FCSTD DOCUMENT  (FreeCAD 1.2R20260429 (Git shallow))
Label: gripper-assembly
License: All rights reserved
LicenseURL: https://en.wikipedia.org/wiki/All_rights_reserved
objects: App::FeaturePython×20, App::Link×15, App::Point×1, Assembly::JointGroup×1, App::DocumentObjectGroup×1, Assembly::AssemblyObject×1
EXTERNAL_REF file=gripper-parts.FCStd obj=Body077
EXTERNAL_REF file=gripper-parts.FCStd obj=Body076
EXTERNAL_REF file=gripper-parts.FCStd obj=Part__Mirroring004
EXTERNAL_REF file=gripper-parts.FCStd obj=Body059
EXTERNAL_REF file=gripper-parts.FCStd obj=Body058
EXTERNAL_REF file=gripper-parts.FCStd obj=Body057
EXTERNAL_REF file=gripper-parts.FCStd obj=Body056
EXTERNAL_REF file=gripper-parts.FCStd obj=Body055
EXTERNAL_REF file=gripper-parts.FCStd obj=Body054
EXTERNAL_REF file=gripper-parts.FCStd obj=Part015
EXTERNAL_REF file=gripper-parts.FCStd obj=Part__Mirroring005
EXTERNAL_REF file=gripper-parts.FCStd obj=Part__Mirroring006
EXTERNAL_REF file=gripper-parts.FCStd obj=Body081
EXTERNAL_REF file=gripper-parts.FCStd obj=Body082
EXTERNAL_REF file=gripper-parts.FCStd obj=Body083

FEATURE [App::Link] Corps008
  LinkPlacement = pos=(-10,-131.392,102.994) rot=(0,0.131358,0.991335;3.14159rad)
  LinkedObject = -> <external gripper-parts.FCStd>#Body077
  Placement = pos=(-10,-131.392,102.994) rot=(0,0.131358,0.991335;3.14159rad)
FEATURE [App::Link] Corps007
  LinkPlacement = pos=(-10,-131.392,102.994) rot=(0,0.131358,0.991335;3.14159rad)
  LinkedObject = -> <external gripper-parts.FCStd>#Body076
  Placement = pos=(-10,-131.392,102.994) rot=(0,0.131358,0.991335;3.14159rad)
FEATURE [App::Link] Clone004__Mirror__5_  label="Clone004 (Mirror #5)"
  LinkPlacement = pos=(10,-190.423,103.07) rot=(0,0.03739,0.999301;3.14159rad)
  LinkedObject = -> <external gripper-parts.FCStd>#Part__Mirroring004
  Placement = pos=(10,-190.423,103.07) rot=(0,0.03739,0.999301;3.14159rad)
FEATURE [App::Link] SupportServoPivot
  LinkPlacement = pos=(-7.5,-131.392,102.994) rot=(0,0.131358,0.991335;3.14159rad)
  LinkedObject = -> <external gripper-parts.FCStd>#Body059
  Placement = pos=(-7.5,-131.392,102.994) rot=(0,0.131358,0.991335;3.14159rad)
FEATURE [App::Link] Corps005
  LinkPlacement = pos=(-26,-178.866,80.5912) rot=(0,-0.307811,0.951448;3.14159rad)
  LinkedObject = -> <external gripper-parts.FCStd>#Body058
  Placement = pos=(-26,-178.866,80.5912) rot=(0,-0.307811,0.951448;3.14159rad)
FEATURE [App::Link] Palonnier
  LinkPlacement = pos=(-26,-168.077,71.1456) rot=(0,-0.230988,0.972957;3.14159rad)
  LinkedObject = -> <external gripper-parts.FCStd>#Body057
  Placement = pos=(-26,-168.077,71.1456) rot=(0,-0.230988,0.972957;3.14159rad)
FEATURE [App::Link] Corps003
  LinkPlacement = pos=(-30,-166.397,111.227) rot=(0,0.09149,0.995806;3.14159rad)
  LinkedObject = -> <external gripper-parts.FCStd>#Body056
  Placement = pos=(-30,-166.397,111.227) rot=(0,0.09149,0.995806;3.14159rad)
FEATURE [App::Link] Corps002
  LinkPlacement = pos=(-30,-190.423,103.07) rot=(0,0.03739,0.999301;3.14159rad)
  LinkedObject = -> <external gripper-parts.FCStd>#Body055
  Placement = pos=(-30,-190.423,103.07) rot=(0,0.03739,0.999301;3.14159rad)
FEATURE [App::Link] SupportServoGripper
  LinkPlacement = pos=(-10,-201.703,81.4943) rot=(0,-0.412163,0.91111;3.14159rad)
  LinkedObject = -> <external gripper-parts.FCStd>#Body054
  Placement = pos=(-10,-201.703,81.4943) rot=(0,-0.412163,0.91111;3.14159rad)
FEATURE [App::Link] MG996
  LinkPlacement = pos=(-24.5,-108.04,39.0451) rot=(-0.577673,-0.576704,0.577673;2.09536rad)
  LinkedObject = -> <external gripper-parts.FCStd>#Part015
  Placement = pos=(-24.5,-108.04,39.0451) rot=(-0.577673,-0.576704,0.577673;2.09536rad)
FEATURE [App::Link] Body079__Mirror__6_  label="Body079 (Mirror #6)"
  LinkPlacement = pos=(10,-166.397,111.227) rot=(0,0.09149,0.995806;3.14159rad)
  LinkedObject = -> <external gripper-parts.FCStd>#Part__Mirroring005
  Placement = pos=(10,-166.397,111.227) rot=(0,0.09149,0.995806;3.14159rad)
FEATURE [App::Link] Body080__Mirror__7_  label="Body080 (Mirror #7)"
  LinkPlacement = pos=(10,-168.077,71.1456) rot=(0,-0.230988,0.972957;3.14159rad)
  LinkedObject = -> <external gripper-parts.FCStd>#Part__Mirroring006
  Placement = pos=(10,-168.077,71.1456) rot=(0,-0.230988,0.972957;3.14159rad)
FEATURE [App::Link] Corps010
  LinkPlacement = pos=(-10,-168.077,71.1456) rot=(0,-0.230988,0.972957;3.14159rad)
  LinkedObject = -> <external gripper-parts.FCStd>#Body081
  Placement = pos=(-10,-168.077,71.1456) rot=(0,-0.230988,0.972957;3.14159rad)
FEATURE [App::Link] Corps011
  LinkPlacement = pos=(0,0,0) rot=(-1,0,0;0.001678rad)
  LinkedObject = -> <external gripper-parts.FCStd>#Body082
  Placement = pos=(0,0,0) rot=(-1,0,0;0.001678rad)
FEATURE [App::Point] Origin001  label="Origine"
  Role = Origin
FEATURE [App::FeaturePython] Joint  label="Fixed032"  # Assembly joint (typed FeaturePython)
  Angle = 0
  AngleMax = 0
  AngleMin = 0
  Detach1 = false
  Detach2 = false
  Distance = 0
  Distance2 = 0
  EnableAngleMax = false
  EnableAngleMin = false
  EnableLengthMax = false
  EnableLengthMin = false
  JointType = 0 (Fixed)
  LengthMax = 0
  LengthMin = 0
  Offset2 = pos=(0,0,0) rot=(0,0,1;3.14159rad)
  Placement1 = pos=(-29.5,-18.5054,-98.3345) rot=(1,0,0;2.87979rad)
  Placement2 = pos=(19.5,-139.141,3) rot=(0,-1,0;3.14159rad)
  Reference1 = -> Corps007 [?Edge127,?Edge127]
  Reference2 = -> Corps011 [?Edge78,?Edge78]
  Suppressed = false
FEATURE [App::FeaturePython] Joint001  label="Fixed033"  # Assembly joint (typed FeaturePython)
  Angle = 0
  AngleMax = 0
  AngleMin = 0
  Detach1 = false
  Detach2 = false
  Distance = 0
  Distance2 = 0
  EnableAngleMax = false
  EnableAngleMin = false
  EnableLengthMax = false
  EnableLengthMin = false
  JointType = 0 (Fixed)
  LengthMax = 0
  LengthMin = 0
  Placement1 = pos=(-9e-16,-50.1695,-70.4616) rot=(0.57735,-0.57735,-0.57735;2.0944rad)
  Placement2 = pos=(-2.5,-50.1695,-70.4616) rot=(0.57735,-0.57735,-0.57735;2.0944rad)
  Reference1 = -> SupportServoPivot [?Edge58,?Edge58]
  Reference2 = -> Corps007 [?Edge94,?Edge94]
  Suppressed = false
FEATURE [App::FeaturePython] Joint002  label="Fixed034"  # Assembly joint (typed FeaturePython)
  Angle = 0
  AngleMax = 0
  AngleMin = 0
  Detach1 = false
  Detach2 = false
  Distance = 0
  Distance2 = 0
  EnableAngleMax = false
  EnableAngleMin = false
  EnableLengthMax = false
  EnableLengthMin = false
  JointType = 0 (Fixed)
  LengthMax = 0
  LengthMin = 0
  Placement1 = pos=(-33.5,-20.5388,-75.1547) rot=(0.57735,-0.57735,-0.57735;2.0944rad)
  Placement2 = pos=(-33.5,-20.5388,-75.1547) rot=(0.57735,-0.57735,-0.57735;2.0944rad)
  Reference1 = -> Corps008 [Edge21,Edge21]
  Reference2 = -> Corps007 [?Edge85,?Edge85]
  Suppressed = false
FEATURE [App::FeaturePython] Joint003  label="Revolute035"  # Assembly joint (typed FeaturePython)
  Angle = 0
  AngleMax = 0
  AngleMin = 0
  Detach1 = false
  Detach2 = false
  Distance = 0
  Distance2 = 0
  EnableAngleMax = false
  EnableAngleMin = false
  EnableLengthMax = false
  EnableLengthMin = false
  JointType = 1 (Revolute)
  LengthMax = 0
  LengthMin = 0
  Placement1 = pos=(-52,-15.6736,-58.9752) rot=(-0.57735,-0.57735,-0.57735;4.18879rad)
  Placement2 = pos=(-36,-15.6736,-58.9752) rot=(0.57735,-0.57735,-0.57735;2.0944rad)
  Reference1 = -> Corps005 [Edge85,Edge85]
  Reference2 = -> Corps008 [Edge93,Edge93]
  Suppressed = false
FEATURE [App::FeaturePython] GroundedJoint  # Assembly grounded joint (typed FeaturePython)
  ObjectToGround = -> Corps011
FEATURE [App::FeaturePython] Joint004  label="Revolute036"  # Assembly joint (typed FeaturePython)
  Angle = 0
  AngleMax = 0
  AngleMin = 0
  Detach1 = false
  Detach2 = false
  Distance = 0
  Distance2 = 0
  EnableAngleMax = false
  EnableAngleMin = false
  EnableLengthMax = false
  EnableLengthMin = false
  JointType = 1 (Revolute)
  LengthMax = 0
  LengthMin = 0
  Placement1 = pos=(-16,-39.201,-55.6603) rot=(-0.57735,-0.57735,-0.57735;4.18879rad)
  Placement2 = pos=(-36,-39.201,-55.6603) rot=(0.57735,-0.57735,-0.57735;2.0944rad)
  Reference1 = -> Body080__Mirror__7_ [Edge49,Edge49]
  Reference2 = -> Corps008 [Edge77,Edge77]
  Suppressed = false
FEATURE [App::FeaturePython] Joint005  label="Fixed036"  # Assembly joint (typed FeaturePython)
  Angle = 0
  AngleMax = 0
  AngleMin = 0
  Detach1 = false
  Detach2 = false
  Distance = 0
  Distance2 = 0
  EnableAngleMax = false
  EnableAngleMin = false
  EnableLengthMax = false
  EnableLengthMin = false
  JointType = 0 (Fixed)
  LengthMax = 0
  LengthMin = 0
  Offset2 = pos=(0,0,0) rot=(0,0,1;3.14159rad)
  Placement1 = pos=(-36,-56.5391,-24.1105) rot=(0.57735,-0.57735,-0.57735;2.0944rad)
  Placement2 = pos=(-16,-56.5391,-24.1105) rot=(-0.57735,0.57735,-0.57735;2.0944rad)
  Reference1 = -> Corps010 [Edge50,Edge50]
  Reference2 = -> Body080__Mirror__7_ [Edge40,Edge40]
  Suppressed = false
FEATURE [App::FeaturePython] Joint006  label="Revolute037"  # Assembly joint (typed FeaturePython)
  Angle = 0
  AngleMax = 0
  AngleMin = 0
  Detach1 = false
  Detach2 = false
  Distance = 0
  Distance2 = 0
  EnableAngleMax = false
  EnableAngleMin = false
  EnableLengthMax = false
  EnableLengthMin = false
  JointType = 1 (Revolute)
  LengthMax = 0
  LengthMin = 0
  Placement1 = pos=(-40,-36.0964,7.29411) rot=(-0.57735,-0.57735,-0.57735;4.18879rad)
  Placement2 = pos=(-56,-36.0964,7.29411) rot=(-0.57735,-0.57735,-0.57735;4.18879rad)
  Reference1 = -> Clone004__Mirror__5_ [Edge72,Edge72]
  Reference2 = -> Corps005 [Edge193,Edge193]
  Suppressed = false
FEATURE [App::FeaturePython] Joint007  label="Revolute038"  # Assembly joint (typed FeaturePython)
  Angle = 0
  AngleMax = 0
  AngleMin = 0
  Detach1 = false
  Detach2 = false
  Distance = 0
  Distance2 = 0
  EnableAngleMax = false
  EnableAngleMin = false
  EnableLengthMax = false
  EnableLengthMin = false
  JointType = 1 (Revolute)
  LengthMax = 0
  LengthMin = 0
  Placement1 = pos=(0,-36.0964,7.29411) rot=(-0.57735,-0.57735,-0.57735;4.18879rad)
  Placement2 = pos=(4,-36.0964,7.29411) rot=(-0.57735,-0.57735,-0.57735;4.18879rad)
  Reference1 = -> Corps002 [Edge72,Edge72]
  Reference2 = -> Corps005 [Edge191,Edge191]
  Suppressed = false
FEATURE [App::FeaturePython] Joint008  label="Revolute039"  # Assembly joint (typed FeaturePython)
  Angle = 0
  AngleMax = 0
  AngleMin = 0
  Detach1 = false
  Detach2 = false
  Distance = 0
  Distance2 = 0
  EnableAngleMax = false
  EnableAngleMin = false
  EnableLengthMax = false
  EnableLengthMin = false
  JointType = 1 (Revolute)
  LengthMax = 0
  LengthMin = 0
  Placement1 = pos=(-20,-34.4956,-23.997) rot=(-0.57735,-0.57735,-0.57735;4.18879rad)
  Placement2 = pos=(-56,-34.4956,-23.997) rot=(-0.57735,-0.57735,-0.57735;4.18879rad)
  Reference1 = -> Body079__Mirror__6_ [Edge87,Edge87]
  Reference2 = -> Corps005 [Edge187,Edge187]
  Suppressed = false
FEATURE [App::FeaturePython] Joint009  label="Revolute040"  # Assembly joint (typed FeaturePython)
  Angle = 0
  AngleMax = 0
  AngleMin = 0
  Detach1 = false
  Detach2 = false
  Distance = 0
  Distance2 = 0
  EnableAngleMax = false
  EnableAngleMin = false
  EnableLengthMax = false
  EnableLengthMin = false
  JointType = 1 (Revolute)
  LengthMax = 0
  LengthMin = 0
  Placement1 = pos=(-20,-61.8186,-11.463) rot=(-0.57735,-0.57735,-0.57735;4.18879rad)
  Placement2 = pos=(-20,-61.8186,-11.463) rot=(-0.57735,-0.57735,-0.57735;4.18879rad)
  Reference1 = -> Body079__Mirror__6_ [Edge86,Edge86]
  Reference2 = -> Body080__Mirror__7_ [Edge57,Edge57]
  Suppressed = false
FEATURE [App::FeaturePython] Joint010  label="Revolute041"  # Assembly joint (typed FeaturePython)
  Angle = 0
  AngleMax = 0
  AngleMin = 0
  Detach1 = false
  Detach2 = false
  Distance = 0
  Distance2 = 0
  EnableAngleMax = false
  EnableAngleMin = false
  EnableLengthMax = false
  EnableLengthMin = false
  JointType = 1 (Revolute)
  LengthMax = 0
  LengthMin = 0
  Placement1 = pos=(0,-34.4956,-23.997) rot=(-0.57735,-0.57735,-0.57735;4.18879rad)
  Placement2 = pos=(4,-34.4956,-23.997) rot=(-0.57735,-0.57735,-0.57735;4.18879rad)
  Reference1 = -> Corps003 [Edge87,Edge87]
  Reference2 = -> Corps005 [Edge185,Edge185]
  Suppressed = false
FEATURE [App::FeaturePython] Joint011  label="Revolute042"  # Assembly joint (typed FeaturePython)
  Angle = 0
  AngleMax = 0
  AngleMin = 0
  Detach1 = false
  Detach2 = false
  Distance = 0
  Distance2 = 0
  EnableAngleMax = false
  EnableAngleMin = false
  EnableLengthMax = false
  EnableLengthMin = false
  JointType = 1 (Revolute)
  LengthMax = 0
  LengthMin = 0
  Placement1 = pos=(-40,-10.5946,-17.3494) rot=(-0.57735,-0.57735,-0.57735;4.18879rad)
  Placement2 = pos=(-20,-10.5946,-24.3494) rot=(-0.57735,-0.57735,-0.57735;4.18879rad)
  Reference1 = -> SupportServoGripper [?Edge250,?Edge250]
  Reference2 = -> Clone004__Mirror__5_ [Edge71,Edge71]
  Suppressed = false
FEATURE [App::FeaturePython] Joint012  label="Revolute043"  # Assembly joint (typed FeaturePython)
  Angle = 0
  AngleMax = 0
  AngleMin = 0
  Detach1 = false
  Detach2 = false
  Distance = 0
  Distance2 = 0
  EnableAngleMax = false
  EnableAngleMin = false
  EnableLengthMax = false
  EnableLengthMin = false
  JointType = 1 (Revolute)
  LengthMax = 0
  LengthMin = 0
  Placement1 = pos=(-20,-10.5946,-47.1305) rot=(-0.57735,-0.57735,-0.57735;4.18879rad)
  Placement2 = pos=(-40,-10.5946,-40.1305) rot=(-0.57735,-0.57735,-0.57735;4.18879rad)
  Reference1 = -> Body079__Mirror__6_ [Edge88,Edge88]
  Reference2 = -> SupportServoGripper [?Edge248,?Edge248]
  Suppressed = false
FEATURE [App::FeaturePython] Joint013  label="Revolute044"  # Assembly joint (typed FeaturePython)
  Angle = 0
  AngleMax = 0
  AngleMin = 0
  Detach1 = false
  Detach2 = false
  Distance = 0
  Distance2 = 0
  EnableAngleMax = false
  EnableAngleMin = false
  EnableLengthMax = false
  EnableLengthMin = false
  JointType = 1 (Revolute)
  LengthMax = 0
  LengthMin = 0
  Placement1 = pos=(0,-10.5946,-24.3494) rot=(-0.57735,-0.57735,-0.57735;4.18879rad)
  Placement2 = pos=(20,-10.5946,-17.3494) rot=(-0.57735,-0.57735,-0.57735;4.18879rad)
  Reference1 = -> Corps002 [Edge71,Edge71]
  Reference2 = -> SupportServoGripper [Edge232,Edge232]
  Suppressed = false
FEATURE [App::FeaturePython] Joint014  label="Revolute046"  # Assembly joint (typed FeaturePython)
  Angle = 0
  AngleMax = 0
  AngleMin = 0
  Detach1 = false
  Detach2 = false
  Distance = 0
  Distance2 = 0
  EnableAngleMax = false
  EnableAngleMin = false
  EnableLengthMax = false
  EnableLengthMin = false
  JointType = 1 (Revolute)
  LengthMax = 0
  LengthMin = 0
  Placement1 = pos=(20,-10.5946,-40.1305) rot=(-0.57735,-0.57735,-0.57735;4.18879rad)
  Placement2 = pos=(0,-10.5946,-47.1305) rot=(-0.57735,-0.57735,-0.57735;4.18879rad)
  Reference1 = -> SupportServoGripper [Edge229,Edge229]
  Reference2 = -> Corps003 [Edge88,Edge88]
  Suppressed = false
FEATURE [App::FeaturePython] Joint015  label="Fixed037"  # Assembly joint (typed FeaturePython)
  Angle = 0
  AngleMax = 0
  AngleMin = 0
  Detach1 = false
  Detach2 = false
  Distance = 0
  Distance2 = 0
  EnableAngleMax = false
  EnableAngleMin = false
  EnableLengthMax = false
  EnableLengthMin = false
  JointType = 0 (Fixed)
  LengthMax = 0
  LengthMin = 0
  Offset2 = pos=(0,0,0) rot=(0,0,1;3.14159rad)
  Placement1 = pos=(3.6e-15,-56.5391,-24.1105) rot=(-0.57735,-0.57735,-0.57735;4.18879rad)
  Placement2 = pos=(16,-56.5391,-24.1105) rot=(-0.57735,-0.57735,0.57735;2.0944rad)
  Reference1 = -> Palonnier [Edge37,Edge37]
  Reference2 = -> Corps010 [Edge22,Edge22]
  Suppressed = false
FEATURE [App::FeaturePython] Joint016  label="Revolute047"  # Assembly joint (typed FeaturePython)
  Angle = 0
  AngleMax = 0
  AngleMin = 0
  Detach1 = false
  Detach2 = false
  Distance = 0
  Distance2 = 0
  EnableAngleMax = false
  EnableAngleMin = false
  EnableLengthMax = false
  EnableLengthMin = false
  JointType = 1 (Revolute)
  LengthMax = 0
  LengthMin = 0
  Placement1 = pos=(4,-61.8186,-11.463) rot=(-0.57735,-0.57735,-0.57735;4.18879rad)
  Placement2 = pos=(0,-61.8186,-11.463) rot=(-0.57735,-0.57735,-0.57735;4.18879rad)
  Reference1 = -> Palonnier [Edge50,Edge50]
  Reference2 = -> Corps003 [Edge86,Edge86]
  Suppressed = false
FEATURE [App::FeaturePython] Joint017  label="Revolute048"  # Assembly joint (typed FeaturePython)
  Angle = 0
  AngleMax = 0
  AngleMin = 0
  Detach1 = false
  Detach2 = false
  Distance = 0
  Distance2 = 0
  EnableAngleMax = false
  EnableAngleMin = false
  EnableLengthMax = false
  EnableLengthMin = false
  JointType = 1 (Revolute)
  LengthMax = 0
  LengthMin = 0
  Placement1 = pos=(14.5,-5,-16) rot=(0,0,1;0rad)
  Placement2 = pos=(-9e-16,-51.9128,-47.0778) rot=(0.57735,-0.57735,-0.57735;2.0944rad)
  Reference1 = -> MG996 [Body041.Edge51,Body041.Edge51]
  Reference2 = -> SupportServoPivot [?Edge61,?Edge61]
  Suppressed = false
FEATURE [App::FeaturePython] Joint018  label="Revolute049"  # Assembly joint (typed FeaturePython)
  Angle = 0
  AngleMax = 0
  AngleMin = 0
  Detach1 = false
  Detach2 = false
  Distance = 0
  Distance2 = 0
  EnableAngleMax = false
  EnableAngleMin = false
  EnableLengthMax = false
  EnableLengthMin = false
  JointType = 1 (Revolute)
  LengthMax = 0
  LengthMin = 0
  Placement1 = pos=(-34.5,5,-16) rot=(0,0,1;0rad)
  Placement2 = pos=(-9e-16,-7.17065,-69.4192) rot=(0.57735,-0.57735,-0.57735;2.0944rad)
  Reference1 = -> MG996 [Body041.Edge38,Body041.Edge38]
  Reference2 = -> SupportServoPivot [?Edge70,?Edge70]
  Suppressed = false
FEATURE [Assembly::JointGroup] Joints
  Group = -> [Joint,Joint001,Joint002,Joint003,GroundedJoint,Joint004,Joint005,Joint006,Joint007,Joint008,Joint009,Joint010,Joint011,Joint012,Joint013,Joint014,Joint015,Joint016,Joint017,Joint018]
FEATURE [App::Link] Corps
  LinkPlacement = pos=(-10,-131.392,102.994) rot=(0,0.131358,0.991335;3.14159rad)
  LinkedObject = -> <external gripper-parts.FCStd>#Body083
  Placement = pos=(-10,-131.392,102.994) rot=(0,0.131358,0.991335;3.14159rad)
FEATURE [App::DocumentObjectGroup] Group  label="PivotPrincipal"
  Group = -> [Corps008,Corps007,Clone004__Mirror__5_,SupportServoPivot,Corps005,Palonnier,Corps003,Corps002,SupportServoGripper,MG996,Body079__Mirror__6_,Body080__Mirror__7_,Corps010,Corps011,Corps]
FEATURE [Assembly::AssemblyObject] Assembly  label="lifter-asm"
  Group = -> [Joints,Corps008,Corps007,Clone004__Mirror__5_,SupportServoPivot,Corps005,Palonnier,Corps003,Corps002,SupportServoGripper,MG996,Body080__Mirror__7_,Body079__Mirror__6_,Corps010,Corps011,Group,Joint,Joint001,Joint002,Joint003,GroundedJoint,Joint004,Joint005,Joint006,Joint007,Joint008,Joint009,Joint010,Joint011,Joint012,Joint013,Joint014,Joint015,Joint016,Joint017,Joint018,Corps]
  Origin = -> Origin
  Type = Assembly

RESOLVED EXTERNAL PARTS (link-assembly join: the EXTERNAL_REF files above that resolve inside this repo's crawl, each included once):
---- part gripper-parts.FCStd = doc fcstd_489b7d980009 (208602 chars; too large to inline — full recipe in that document) ----
